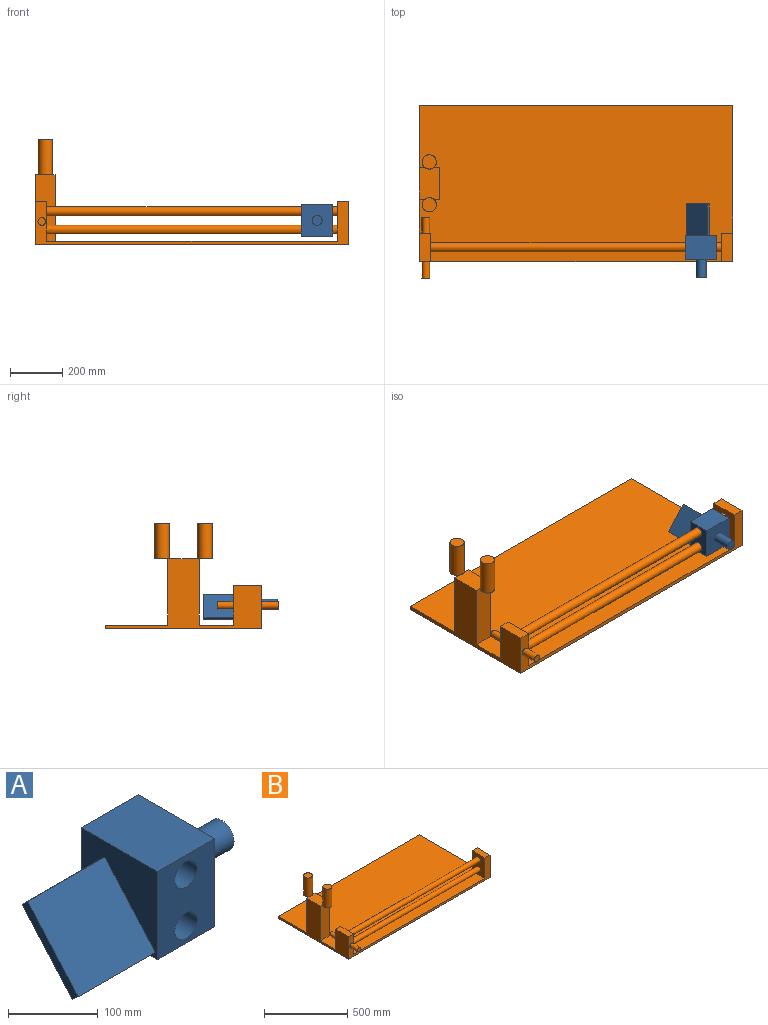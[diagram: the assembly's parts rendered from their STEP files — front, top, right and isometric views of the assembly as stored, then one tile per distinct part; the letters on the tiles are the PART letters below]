
ASSEMBLY  parts=2 mates=1
PART A: 15 faces, bbox 283.1x120x120 mm
  f0: plane 120x120mm, normal (-1,0,0), area 12960mm2, adj f1,f2,f3,f4,f8,f9,f10,f11
  f1: plane 120x90mm, normal (0,0,-1), area 10800mm2, adj f0,f2,f4,f5
  f2: plane 120x90mm, normal (0,1,0), area 8875.8mm2, adj f0,f1,f3,f5,f6,f7
  f3: plane 120x90mm, normal (0,0,1), area 10800mm2, adj f0,f2,f4,f5
  f4: plane 120x90mm, normal (0,-1,0), area 8875.8mm2, adj f0,f1,f3,f5,f6,f7
  f5: plane 120x120mm, normal (1,0,0), area 13251.2mm2, adj f1,f2,f3,f4,f13
  f6: cylinder r=17.5mm len=120mm, axis (0,-1,0), area 13194.7mm2, adj f2,f4
  f7: cylinder r=17.5mm len=120mm, axis (0,-1,0), area 13194.7mm2, adj f2,f4
  f8: plane 121.6x90.09mm, normal (0,-0.75,0.66), area 14592mm2, adj f0,f9,f11,f12
  f9: plane 121.6x9.01mm, normal (0,0.66,0.75), area 1459.2mm2, adj f0,f8,f10,f12
  f10: plane 121.6x90.09mm, normal (0,0.75,-0.66), area 14592mm2, adj f0,f9,f11,f12
  f11: plane 121.6x9.01mm, normal (0,-0.66,-0.75), area 1459.2mm2, adj f0,f8,f10,f12
  f12: plane 98.01x88.28mm, normal (-1,0,0), area 1440mm2, adj f8,f9,f10,f11
  f13: cylinder r=19.12mm len=71.5mm, axis (-1,0,0), area 8590.9mm2, adj f5,f14
  f14: plane 38.25x38.25mm, normal (1,0,0), area 1148.8mm2, adj f13
PART B: 30 faces, bbox 1200x665x406 mm
  f0: plane 1200x600mm, normal (0,0,1), area 701597.3mm2, adj f2,f3,f4,f5,f7,f8,f9,f16
  f1: plane 120x75.17mm, normal (0,0,1), area 8806.9mm2, adj f5,f7,f8,f9,f10,f14
  f2: plane 1200x165mm, normal (0,-1,0), area 30123.9mm2, adj f0,f3,f5,f6,f17,f18,f20,f21
  f3: plane 600x165mm, normal (1,0,0), area 25497.6mm2, adj f0,f2,f4,f6,f19,f21
  f4: plane 1200x15mm, normal (0,1,0), area 18000mm2, adj f0,f3,f5,f6
  f5: plane 600x269mm, normal (-1,0,0), area 55977.6mm2, adj f0,f1,f2,f4,f6,f7,f8,f16
  f6: plane 1200x600mm, normal (0,0,-1), area 720000mm2, adj f2,f3,f4,f5
  f7: plane 254x75.17mm, normal (0,1,0), area 19093mm2, adj f0,f1,f5,f9,f12
  f8: plane 254x75.17mm, normal (0,-1,0), area 19093mm2, adj f0,f1,f5,f9,f13
  f9: plane 254x120mm, normal (1,0,0), area 30480mm2, adj f0,f1,f7,f8
  f10: cylinder r=27.29mm len=137mm, axis (0,0,-1), area 23495.3mm2, adj f1,f11,f12
  f11: plane 54.59x54.59mm, normal (0,0,1), area 2340.5mm2, adj f10
  f12: plane 54.59x49.6mm, normal (0,0,-1), area 2233.8mm2, adj f7,f10
  f13: plane 54.59x49.6mm, normal (0,0,-1), area 2233.8mm2, adj f8,f14
  f14: cylinder r=27.29mm len=137mm, axis (0,0,-1), area 23495.3mm2, adj f1,f13,f15
  f15: plane 54.59x54.59mm, normal (0,0,1), area 2340.5mm2, adj f14
  f16: plane 150x42.65mm, normal (0,1,0), area 5725.9mm2, adj f0,f5,f17,f18,f27
  f17: plane 150x109.98mm, normal (1,0,0), area 16497.6mm2, adj f0,f2,f16,f18
  f18: plane 109.98x42.65mm, normal (0,0,1), area 4691.2mm2, adj f2,f5,f16,f17
  f19: plane 150x42.65mm, normal (0,1,0), area 6398mm2, adj f0,f3,f20,f21
  f20: plane 150x109.98mm, normal (-1,0,0), area 14573.4mm2, adj f0,f2,f19,f21,f22,f24
  f21: plane 109.98x42.65mm, normal (0,0,1), area 4691.2mm2, adj f2,f3,f19,f20
  f22: cylinder r=17.5mm len=1114mm, axis (1,0,0), area 122490.7mm2, adj f20,f23
  f23: plane 35x35mm, normal (-1,0,0), area 962.1mm2, adj f22
  f24: cylinder r=17.5mm len=1114mm, axis (1,0,0), area 122490.7mm2, adj f20,f25
  f25: plane 35x35mm, normal (-1,0,0), area 962.1mm2, adj f24
  f26: plane 29.25x29.25mm, normal (0,1,0), area 672.1mm2, adj f27
  f27: cylinder r=14.63mm len=61.02mm, axis (0,1,0), area 5607.5mm2, adj f16,f26
  f28: cylinder r=14.63mm len=65mm, axis (0,1,0), area 5973.7mm2, adj f2,f29
  f29: plane 29.25x29.25mm, normal (0,-1,0), area 672.1mm2, adj f28
PLACE A rot(axis=(0,0,-1),90deg) t=(441.5,-31.92,69.85)mm
PLACE B t=(-38.23,168.09,-24.33)mm fixed
MATE slider A.f7 <-> B.f22  axis (-1,0,0) through (381.5,-76.92,103.85)mm
